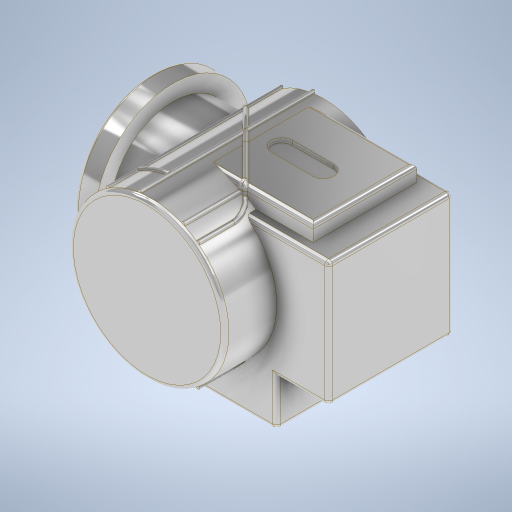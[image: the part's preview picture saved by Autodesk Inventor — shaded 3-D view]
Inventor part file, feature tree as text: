
AUTODESK INVENTOR PART (.ipt)
format: ipt  version: 2023 (Build 270158000, 158)  size: 870,912 bytes
history: native  units: mm
features: sketch x16, extrude x12, other x9, fillet x5, sweep x5, loft x1
ambient origin geometry x8: Origin, YZ Plane, XZ Plane, XY Plane, X Axis, Y Axis, Z Axis, Center Point
bodies: Body1 (feature_tree)
feature tree (48):
  other  "솔리드1"
  extrude  "돌출1"  Depth=75.0mm
  other  "작업 평면1"
  extrude  "돌출2"  Depth=85.0mm TaperAngle=0.0deg
  extrude  "돌출3"  Depth=60.0mm
  other  "작업 평면2"
  loft  "로프트1"
  fillet  "모깎기2"  Radius=5.0mm
  fillet  "모깎기3"  Radius=30.0mm
  other  "작업 평면3"
  other  "작업 평면4"
  extrude  "돌출4"  Depth=75.0mm
  extrude  "돌출5"  Depth=10.0mm TaperAngle=0.0deg
  fillet  "모깎기4"  Radius=10.0mm
  extrude  "돌출6"  Depth=50.0mm
  fillet  "모깎기5"  Radius=60.0mm
  sketch  "3D 스케치3"
  other  "작업 평면5"
  sketch  "스케치12"
  sweep  "스윕1"
  sweep  "스윕2"
  sweep  "스윕3"
  sweep  "스윕4"
  other  "작업 평면6"
  sweep  "스윕5"
  other  "작업 평면7"
  sketch  "스케치14"
  extrude  "돌출8"  Depth=60.0mm
  extrude  "돌출10"  Depth=60.0mm
  extrude  "돌출11"  Depth=25.0mm TaperAngle=0.0deg
  extrude  "돌출12"  Depth=15.0mm
  extrude  "돌출13"  Depth=88.0mm
  extrude  "돌출14"  Depth=22.0mm
  fillet  "모깎기7"  Radius=15.0mm
  sketch  "스케치1"
  sketch  "스케치2"
  sketch  "스케치3"
  sketch  "스케치6"
  sketch  "스케치7"
  sketch  "스케치9"
  sketch  "스케치11"
  other  "곡면에 투영3"
  sketch  "스케치13"
  sketch  "스케치15"
  sketch  "스케치18"
  sketch  "스케치19"
  sketch  "스케치20"
  sketch  "스케치21"
